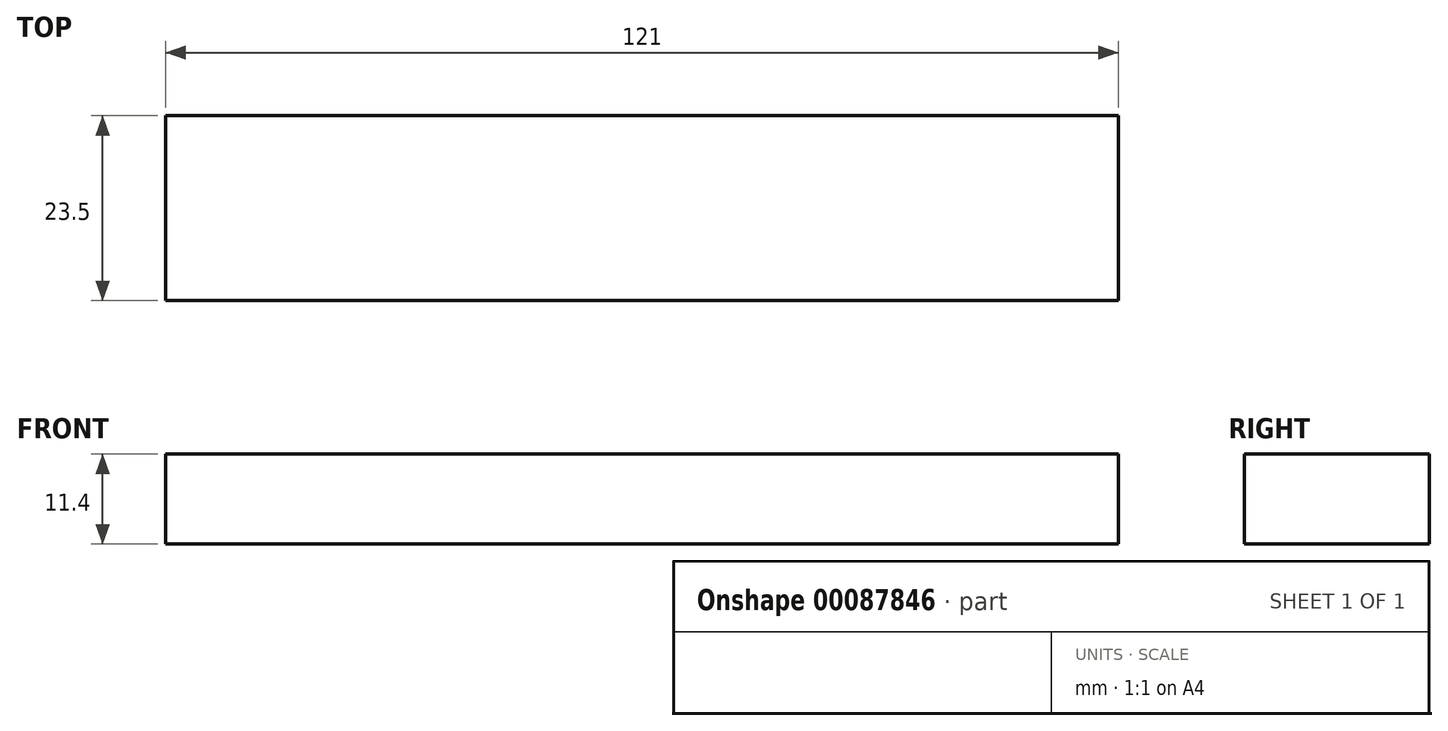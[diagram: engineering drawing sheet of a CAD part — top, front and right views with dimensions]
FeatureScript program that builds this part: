
annotation { "Feature Type Name" : "Feature", "Feature Type Description" : "" }
export const myFeature = defineFeature(function(context is Context, id is Id, definition is map)
    precondition{}
    {
        {
            var Q0;
            Q0=qCreatedBy(makeId("Top.planeOp"),FACE);
            var sketch = newSketch(context, id + "F0", { "sketchPlane" : qUnion([Q0])});
            skLineSegment(sketch, "E0.bottom", {"start": v(60.5, 11.75) * mm, "end": v(-60.5, 11.75) * mm});
            skLineSegment(sketch, "E0.top", {"start": v(60.5, -11.75) * mm, "end": v(-60.5, -11.75) * mm});
            skLineSegment(sketch, "E0.left", {"start": v(60.5, 11.75) * mm, "end": v(60.5, -11.75) * mm});
            skLineSegment(sketch, "E0.right", {"start": v(-60.5, 11.75) * mm, "end": v(-60.5, -11.75) * mm});
            skPoint(sketch, "E0.middle", {"position": v(0, 0) * mm});
            skCircle(sketch, "E1", {"center": v(55.45, 8.1) * mm, "radius": 1.65 * mm});
            skLineSegment(sketch, "E2.bottom", {"start": v(-56.85, 9.75) * mm, "end": v(-52.35, 9.75) * mm});
            skLineSegment(sketch, "E2.top", {"start": v(-56.85, 6.45) * mm, "end": v(-52.35, 6.45) * mm});
            skLineSegment(sketch, "E2.left", {"start": v(-58.5, 8.1) * mm, "end": v(-58.5, 8.1) * mm});
            skLineSegment(sketch, "E2.right", {"start": v(-50.7, 8.1) * mm, "end": v(-50.7, 8.1) * mm});
            skPoint(sketch, "E3.visualSharp", {"position": v(-50.7, 9.75) * mm});
            skArc(sketch, "E3.filletArc", {"start": v(-50.7, 8.1) * mm, "mid": v(-51.18, 9.27) * mm, "end": v(-52.35, 9.75) * mm});
            skPoint(sketch, "E4.visualSharp", {"position": v(-50.7, 6.45) * mm});
            skArc(sketch, "E4.filletArc", {"start": v(-52.35, 6.45) * mm, "mid": v(-51.18, 6.93) * mm, "end": v(-50.7, 8.1) * mm});
            skPoint(sketch, "E5.visualSharp", {"position": v(-58.5, 9.75) * mm});
            skArc(sketch, "E5.filletArc", {"start": v(-56.85, 9.75) * mm, "mid": v(-58.02, 9.27) * mm, "end": v(-58.5, 8.1) * mm});
            skPoint(sketch, "E6.visualSharp", {"position": v(-58.5, 6.45) * mm});
            skArc(sketch, "E6.filletArc", {"start": v(-58.5, 8.1) * mm, "mid": v(-58.02, 6.93) * mm, "end": v(-56.85, 6.45) * mm});
            skSolve(sketch);
        }
        {
            var Q0;
            Q0=makeQuery(id+"F0.imprint","IMPRINT",FACE,{"disambiguationData":[TD([[makeQuery(id+"F0.imprint","IMPRINT",EDGE,{"derivedFrom":sQuery(id+"F0.wireOp",EDGE,"E0.bottom")}),1.0]])]});
            extrude(context, id + "F1", {"entities" : qUnion([Q0]), "depth" : 1.6 * mm});
        }
        {
            var Q0;
            Q0=makeQuery(id+"F0.imprint","IMPRINT",FACE,{"disambiguationData":[TD([[makeQuery(id+"F0.imprint","IMPRINT",EDGE,{"derivedFrom":sQuery(id+"F0.wireOp",EDGE,"E0.bottom")}),1.0]])]});
            var sketch = newSketch(context, id + "F2", { "sketchPlane" : qUnion([Q0])});
            skLineSegment(sketch, "E7.bottom", {"start": v(-60.5, 11.75) * mm, "end": v(60.5, 11.75) * mm});
            skLineSegment(sketch, "E7.top", {"start": v(-60.5, -11.75) * mm, "end": v(60.5, -11.75) * mm});
            skLineSegment(sketch, "E7.left", {"start": v(-60.5, 11.75) * mm, "end": v(-60.5, -11.75) * mm});
            skLineSegment(sketch, "E7.right", {"start": v(60.5, 11.75) * mm, "end": v(60.5, -11.75) * mm});
            skSolve(sketch);
        }
        {
            var Q0;
            Q0 = qSketchRegion(id + "F2", true);
            extrude(context, id + "F3", {"entities" : qUnion([Q0]), "depth" : (13 - 1.6) * mm});
        }
        {
            var Q0;
            Q0=makeQuery(id+"F1.opExtrude","CAP_FACE",FACE,{"disambiguationData":[OSD([sQuery(id+"F0.wireOp",EDGE,"E0.bottom"),sQuery(id+"F0.wireOp",EDGE,"E0.top"),sQuery(id+"F0.wireOp",EDGE,"E0.left"),sQuery(id+"F0.wireOp",EDGE,"E0.right"),sQuery(id+"F0.wireOp",EDGE,"E1"),sQuery(id+"F0.wireOp",EDGE,"E2.bottom"),sQuery(id+"F0.wireOp",EDGE,"E2.top"),sQuery(id+"F0.wireOp",EDGE,"E3.filletArc"),sQuery(id+"F0.wireOp",EDGE,"E4.filletArc"),sQuery(id+"F0.wireOp",EDGE,"E5.filletArc"),sQuery(id+"F0.wireOp",EDGE,"E6.filletArc")])],"isStart":false});
            var sketch = newSketch(context, id + "F4", { "sketchPlane" : qUnion([Q0])});
            skLineSegment(sketch, "E8.bottom", {"start": v(33.77, 10.74) * mm, "end": v(45.98, 10.74) * mm});
            skLineSegment(sketch, "E8.top", {"start": v(33.77, 4.6) * mm, "end": v(45.98, 4.6) * mm});
            skLineSegment(sketch, "E8.left", {"start": v(33.77, 10.74) * mm, "end": v(33.77, 4.6) * mm});
            skLineSegment(sketch, "E8.right", {"start": v(45.98, 10.74) * mm, "end": v(45.98, 4.6) * mm});
            skLineSegment(sketch, "E9.bottom", {"start": v(-59.67, -4.3) * mm, "end": v(-51.95, -4.3) * mm});
            skLineSegment(sketch, "E9.top", {"start": v(-59.67, -9.55) * mm, "end": v(-51.95, -9.55) * mm});
            skLineSegment(sketch, "E9.left", {"start": v(-59.67, -4.3) * mm, "end": v(-59.67, -9.55) * mm});
            skLineSegment(sketch, "E9.right", {"start": v(-51.95, -4.3) * mm, "end": v(-51.95, -9.55) * mm});
            skSolve(sketch);
        }
        {
            var Q0;
            Q0 = qSketchRegion(id + "F4", true);
            extrude(context, id + "F5", {"entities" : qUnion([Q0]), "operationType" : NewBodyOperationType.ADD, "depth" : 6 * mm});
        }
    });
